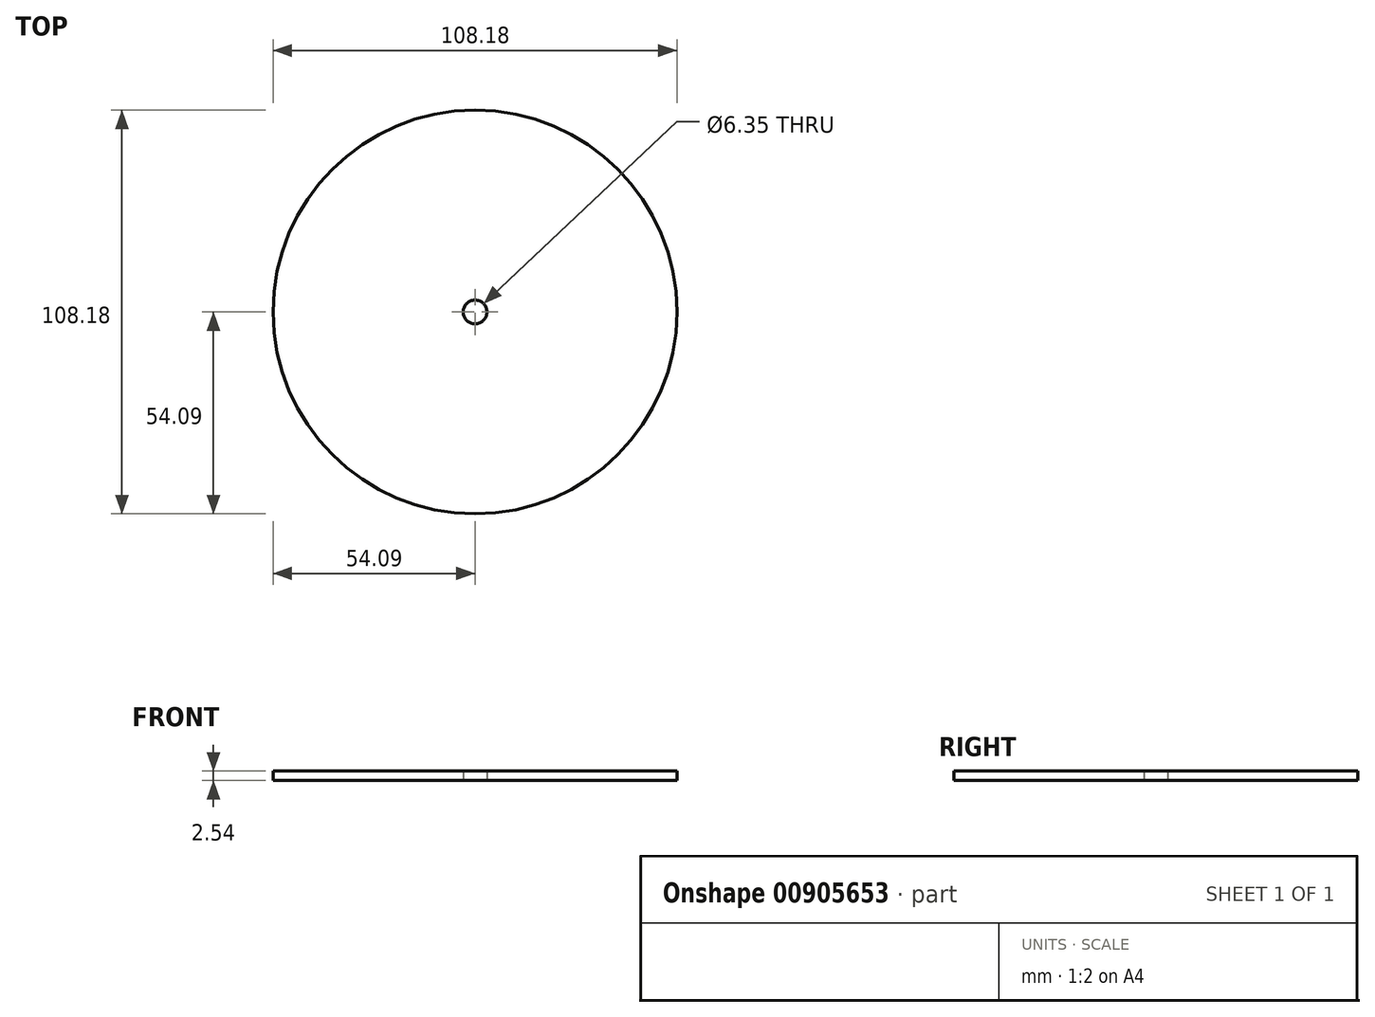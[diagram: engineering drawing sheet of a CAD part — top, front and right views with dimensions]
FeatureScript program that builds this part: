
annotation { "Feature Type Name" : "Feature", "Feature Type Description" : "" }
export const myFeature = defineFeature(function(context is Context, id is Id, definition is map)
    precondition{}
    {
        {
            var Q0;
            Q0=qCreatedBy(makeId("Top.planeOp"),FACE);
            var sketch = newSketch(context, id + "F0", { "sketchPlane" : qUnion([Q0])});
            skCircle(sketch, "E0", {"center": v(0, 0) * mm, "radius": 54.1 * mm});
            skSolve(sketch);
        }
        {
            var Q0;
            Q0=makeQuery(id+"F0.imprint","IMPRINT",FACE,{"disambiguationData":[TD([[makeQuery(id+"F0.imprint","IMPRINT",EDGE,{"derivedFrom":sQuery(id+"F0.wireOp",EDGE,"E0")}),1.0]])]});
            extrude(context, id + "F1", {"entities" : qUnion([Q0]), "depth" : 2.54 * mm, "offsetDistance" : 25.4 * mm});
        }
        {
            var Q0;
            Q0=qCreatedBy(makeId("Top.planeOp"),FACE);
            var sketch = newSketch(context, id + "F2", { "sketchPlane" : qUnion([Q0])});
            skCircle(sketch, "E1", {"center": v(0, 0) * mm, "radius": 3.1 * mm});
            skSolve(sketch);
        }
        {
            var Q0;
            Q0=sQuery(id+"F2.wireOp",VERTEX,"E1.center");
            var Q1;
            Q1=makeQuery(id+"F1.opExtrude","SWEPT_BODY",BODY,{"disambiguationData":[OSD([sQuery(id+"F0.wireOp",EDGE,"E0")])]});
            hole(context, id + "F3", {"style" : HoleStyle.SIMPLE, "endStyle" : HoleEndStyle.THROUGH, "oppositeDirection" : true, "holeDiameter" : 6.35 * mm, "majorDiameter" : 6.35 * mm, "isTappedThrough" : true, "tappedDepth" : 12.7 * mm, "tapClearance" : 3, "locations" : qUnion([Q0]), "scope" : qUnion([Q1])});
        }
    });
